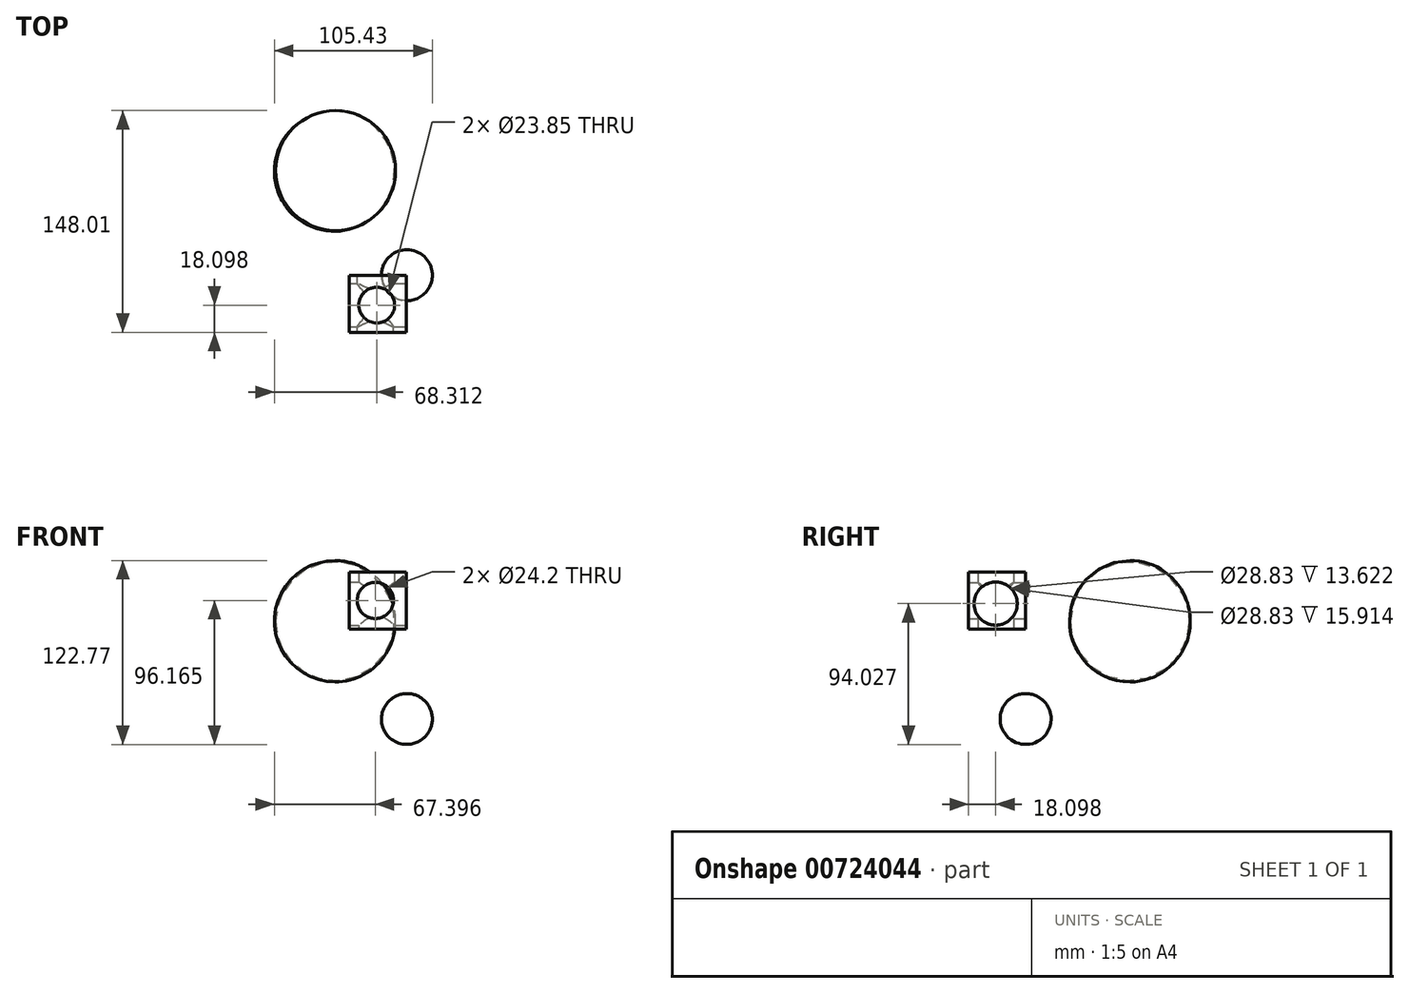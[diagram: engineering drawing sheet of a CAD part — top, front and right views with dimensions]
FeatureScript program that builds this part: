
annotation { "Feature Type Name" : "Feature", "Feature Type Description" : "" }
export const myFeature = defineFeature(function(context is Context, id is Id, definition is map)
    precondition{}
    {
        {
            var Q0;
            Q0=qCreatedBy(makeId("Front.planeOp"),FACE);
            var sketch = newSketch(context, id + "F0", { "sketchPlane" : qUnion([Q0])});
            skLineSegment(sketch, "E0.bottom", {"start": v(23.3, -5.14) * mm, "end": v(-14.8, -5.14) * mm});
            skLineSegment(sketch, "E0.top", {"start": v(23.3, 32.96) * mm, "end": v(-14.8, 32.96) * mm});
            skLineSegment(sketch, "E0.left", {"start": v(23.3, -5.14) * mm, "end": v(23.3, 32.96) * mm});
            skLineSegment(sketch, "E0.right", {"start": v(-14.8, -5.14) * mm, "end": v(-14.8, 32.96) * mm});
            skSolve(sketch);
        }
        {
            var Q0;
            Q0 = qSketchRegion(id + "F0", true);
            extrude(context, id + "F1", {"entities" : qUnion([Q0]), "depth" : 38.1 * mm, "offsetDistance" : 25.4 * mm});
        }
        {
            var Q0;
            Q0=makeQuery(id+"F1.opExtrude","SWEPT_FACE",FACE,{"disambiguationData":[OSD([sQuery(id+"F0.wireOp",EDGE,"E0.bottom")])]});
            var sketch = newSketch(context, id + "F2", { "sketchPlane" : qUnion([Q0])});
            skCircle(sketch, "E1", {"center": v(3.51, 20) * mm, "radius": 11.93 * mm});
            skSolve(sketch);
        }
        {
            var Q0;
            Q0=makeQuery(id+"F2.imprint","IMPRINT",FACE,{"disambiguationData":[TD([[makeQuery(id+"F2.imprint","IMPRINT",EDGE,{"derivedFrom":sQuery(id+"F2.wireOp",EDGE,"E1")}),1.0]])]});
            extrude(context, id + "F3", {"entities" : qUnion([Q0]), "operationType" : NewBodyOperationType.REMOVE, "endBound" : BoundingType.THROUGH_ALL, "oppositeDirection" : true, "depth" : 25.4 * mm, "offsetDistance" : 25.4 * mm});
        }
        {
            var Q0;
            Q0=makeQuery(id+"F1.opExtrude","SWEPT_FACE",FACE,{"disambiguationData":[OSD([sQuery(id+"F0.wireOp",EDGE,"E0.left")])]});
            var sketch = newSketch(context, id + "F4", { "sketchPlane" : qUnion([Q0])});
            skCircle(sketch, "E2", {"center": v(-20, 11.76) * mm, "radius": 14.41 * mm});
            skSolve(sketch);
        }
        {
            var Q0;
            Q0=makeQuery(id+"F4.imprint","IMPRINT",FACE,{"disambiguationData":[TD([[makeQuery(id+"F4.imprint","IMPRINT",EDGE,{"derivedFrom":sQuery(id+"F4.wireOp",EDGE,"E2")}),1.0]])]});
            extrude(context, id + "F5", {"entities" : qUnion([Q0]), "operationType" : NewBodyOperationType.REMOVE, "endBound" : BoundingType.THROUGH_ALL, "oppositeDirection" : true, "depth" : 25.4 * mm, "offsetDistance" : 25.4 * mm});
        }
        {
            var Q0;
            Q0=makeQuery(id+"F1.opExtrude","CAP_FACE",FACE,{"disambiguationData":[OSD([sQuery(id+"F0.wireOp",EDGE,"E0.bottom"),sQuery(id+"F0.wireOp",EDGE,"E0.top"),sQuery(id+"F0.wireOp",EDGE,"E0.left"),sQuery(id+"F0.wireOp",EDGE,"E0.right")])],"isStart":true});
            var sketch = newSketch(context, id + "F6", { "sketchPlane" : qUnion([Q0])});
            skCircle(sketch, "E3", {"center": v(-2.6, 13.9) * mm, "radius": 12.1 * mm});
            skSolve(sketch);
        }
        {
            var Q0;
            Q0 = qSketchRegion(id + "F6", true);
            extrude(context, id + "F7", {"entities" : qUnion([Q0]), "operationType" : NewBodyOperationType.REMOVE, "endBound" : BoundingType.THROUGH_ALL, "oppositeDirection" : true, "depth" : 25.4 * mm, "offsetDistance" : 25.4 * mm});
        }
        {
            var Q0;
            Q0=qCreatedBy(makeId("Front.planeOp"),FACE);
            var sketch = newSketch(context, id + "F8", { "sketchPlane" : qUnion([Q0])});
            skCircle(sketch, "E4", {"center": v(23.72, -65.23) * mm, "radius": 16.9 * mm});
            skLineSegment(sketch, "E5", {"start": v(12.69, -52.42) * mm, "end": v(34.6, -78.17) * mm});
            skSolve(sketch);
        }
        {
            var Q0;
            {var subQ0=sQuery(id+"F8.wireOp",EDGE,"E5");Q0=makeQuery(id+"F8.imprint","IMPRINT",FACE,{"disambiguationData":[TD([[makeQuery(id+"F8.imprint","IMPRINT",EDGE,{"derivedFrom":subQ0}),1.0]])]});}
            var Q1;
            Q1=sQuery(id+"F8.wireOp",EDGE,"E5");
            revolve(context, id + "F9", {"surfaceOperationType" : NewSurfaceOperationType.NEW, "entities" : qUnion([Q0]), "axis" : qUnion([Q1]), "revolveType" : RevolveType.FULL});
        }
        {
            var Q0;
            Q0=qCreatedBy(makeId("Top.planeOp"),FACE);
            var sketch = newSketch(context, id + "F10", { "sketchPlane" : qUnion([Q0])});
            skCircle(sketch, "E6", {"center": v(-24.76, 69.39) * mm, "radius": 40.04 * mm});
            skLineSegment(sketch, "E7", {"start": v(-3.3, 35.6) * mm, "end": v(-45.44, 103.67) * mm});
            skSolve(sketch);
        }
        {
            var Q0;
            {var subQ0=sQuery(id+"F10.wireOp",EDGE,"E7");Q0=makeQuery(id+"F10.imprint","IMPRINT",FACE,{"disambiguationData":[TD([[makeQuery(id+"F10.imprint","IMPRINT",EDGE,{"derivedFrom":subQ0}),-1.0]])]});}
            var Q1;
            Q1=sQuery(id+"F10.wireOp",EDGE,"E7");
            revolve(context, id + "F11", {"surfaceOperationType" : NewSurfaceOperationType.NEW, "entities" : qUnion([Q0]), "axis" : qUnion([Q1]), "revolveType" : RevolveType.FULL});
        }
    });
